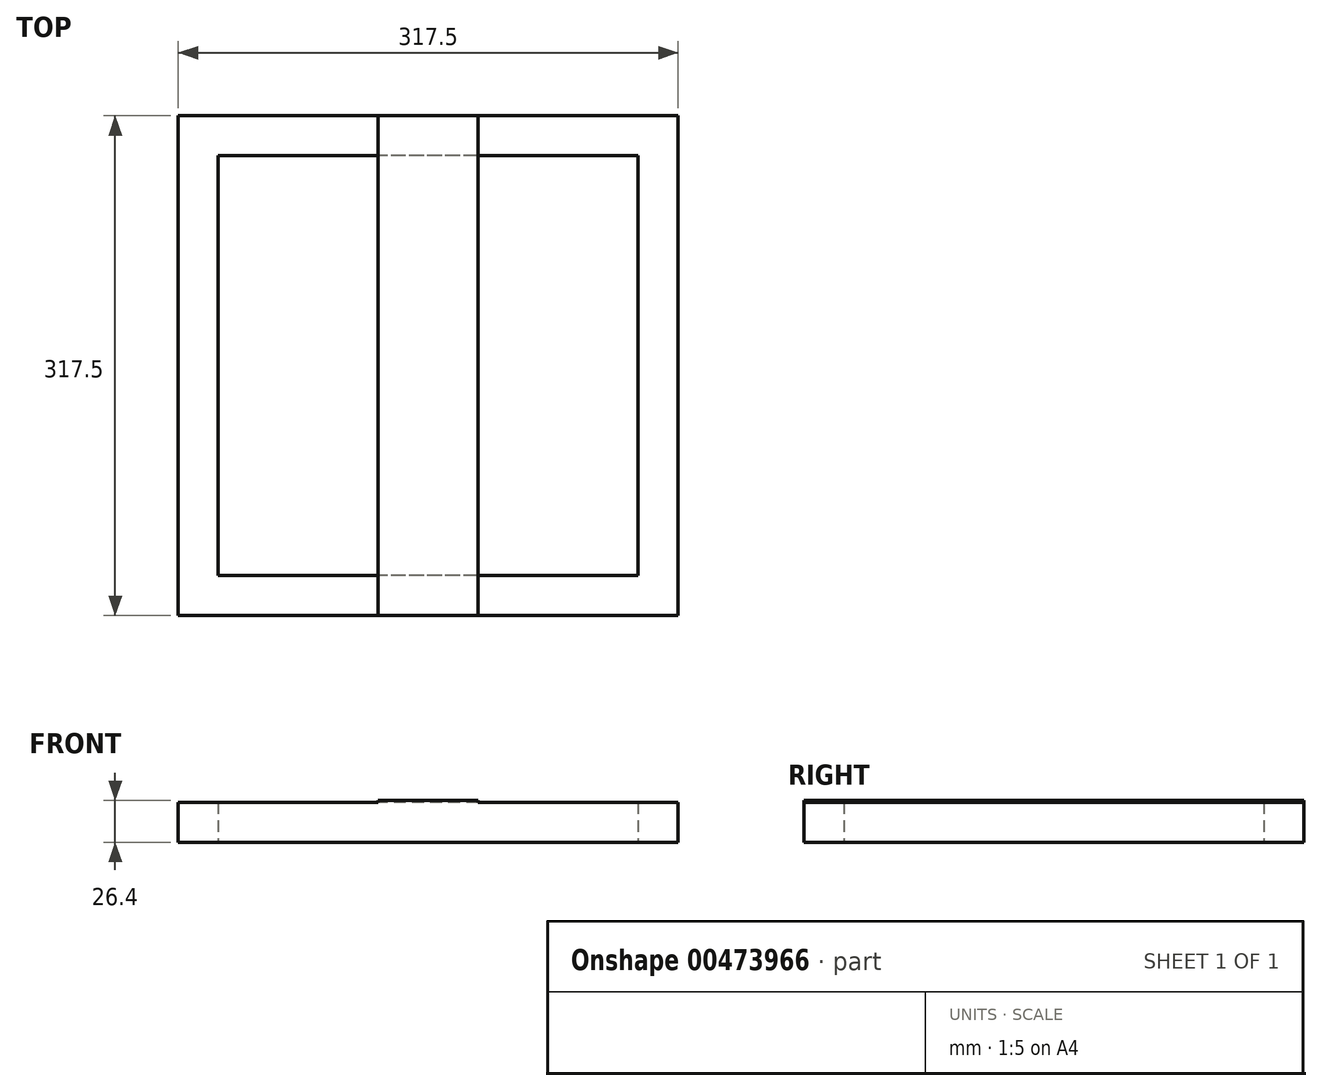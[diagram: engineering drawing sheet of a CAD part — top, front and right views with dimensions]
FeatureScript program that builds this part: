
annotation { "Feature Type Name" : "Feature", "Feature Type Description" : "" }
export const myFeature = defineFeature(function(context is Context, id is Id, definition is map)
    precondition{}
    {
        {
            var Q0;
            Q0=qCreatedBy(makeId("Top.planeOp"),FACE);
            var sketch = newSketch(context, id + "F0", { "sketchPlane" : qUnion([Q0])});
            skLineSegment(sketch, "E0.bottom", {"start": v(158.75, -158.75) * mm, "end": v(-158.75, -158.75) * mm});
            skLineSegment(sketch, "E0.top", {"start": v(158.75, 158.75) * mm, "end": v(-158.75, 158.75) * mm});
            skLineSegment(sketch, "E0.left", {"start": v(158.75, -158.75) * mm, "end": v(158.75, 158.75) * mm});
            skLineSegment(sketch, "E0.right", {"start": v(-158.75, -158.75) * mm, "end": v(-158.75, 158.75) * mm});
            skPoint(sketch, "E0.middle", {"position": v(0, 0) * mm});
            skLineSegment(sketch, "E1.0", {"start": v(133.35, 133.35) * mm, "end": v(-133.35, 133.35) * mm});
            skLineSegment(sketch, "E1.1", {"start": v(133.35, -133.35) * mm, "end": v(133.35, 133.35) * mm});
            skLineSegment(sketch, "E1.2", {"start": v(133.35, -133.35) * mm, "end": v(-133.35, -133.35) * mm});
            skLineSegment(sketch, "E1.3", {"start": v(-133.35, -133.35) * mm, "end": v(-133.35, 133.35) * mm});
            skSolve(sketch);
        }
        {
            var Q0;
            Q0=makeQuery(id+"F0.imprint","IMPRINT",FACE,{"disambiguationData":[TD([[makeQuery(id+"F0.imprint","IMPRINT",EDGE,{"derivedFrom":sQuery(id+"F0.wireOp",EDGE,"E0.bottom")}),-1.0]])]});
            extrude(context, id + "F1", {"entities" : qUnion([Q0]), "depth" : 25.4 * mm});
        }
        {
            var Q0;
            Q0=makeQuery(id+"F1.opExtrude","CAP_FACE",FACE,{"disambiguationData":[OSD([sQuery(id+"F0.wireOp",EDGE,"E0.bottom"),sQuery(id+"F0.wireOp",EDGE,"E0.top"),sQuery(id+"F0.wireOp",EDGE,"E0.left"),sQuery(id+"F0.wireOp",EDGE,"E0.right"),sQuery(id+"F0.wireOp",EDGE,"E1.0"),sQuery(id+"F0.wireOp",EDGE,"E1.1"),sQuery(id+"F0.wireOp",EDGE,"E1.2"),sQuery(id+"F0.wireOp",EDGE,"E1.3")])],"isStart":false});
            var sketch = newSketch(context, id + "F2", { "sketchPlane" : qUnion([Q0])});
            skLineSegment(sketch, "E2.bottom", {"start": v(-31.75, 158.75) * mm, "end": v(31.75, 158.75) * mm});
            skLineSegment(sketch, "E2.top", {"start": v(-31.75, -158.75) * mm, "end": v(31.75, -158.75) * mm});
            skLineSegment(sketch, "E2.left", {"start": v(-31.75, 158.75) * mm, "end": v(-31.75, -158.75) * mm});
            skLineSegment(sketch, "E2.right", {"start": v(31.75, 158.75) * mm, "end": v(31.75, -158.75) * mm});
            skPoint(sketch, "E2.middle", {"position": v(0, 0) * mm});
            skSolve(sketch);
        }
        {
            var Q0;
            Q0 = qSketchRegion(id + "F2", true);
            extrude(context, id + "F3", {"entities" : qUnion([Q0]), "operationType" : NewBodyOperationType.ADD, "depth" : 1 * mm});
        }
    });
